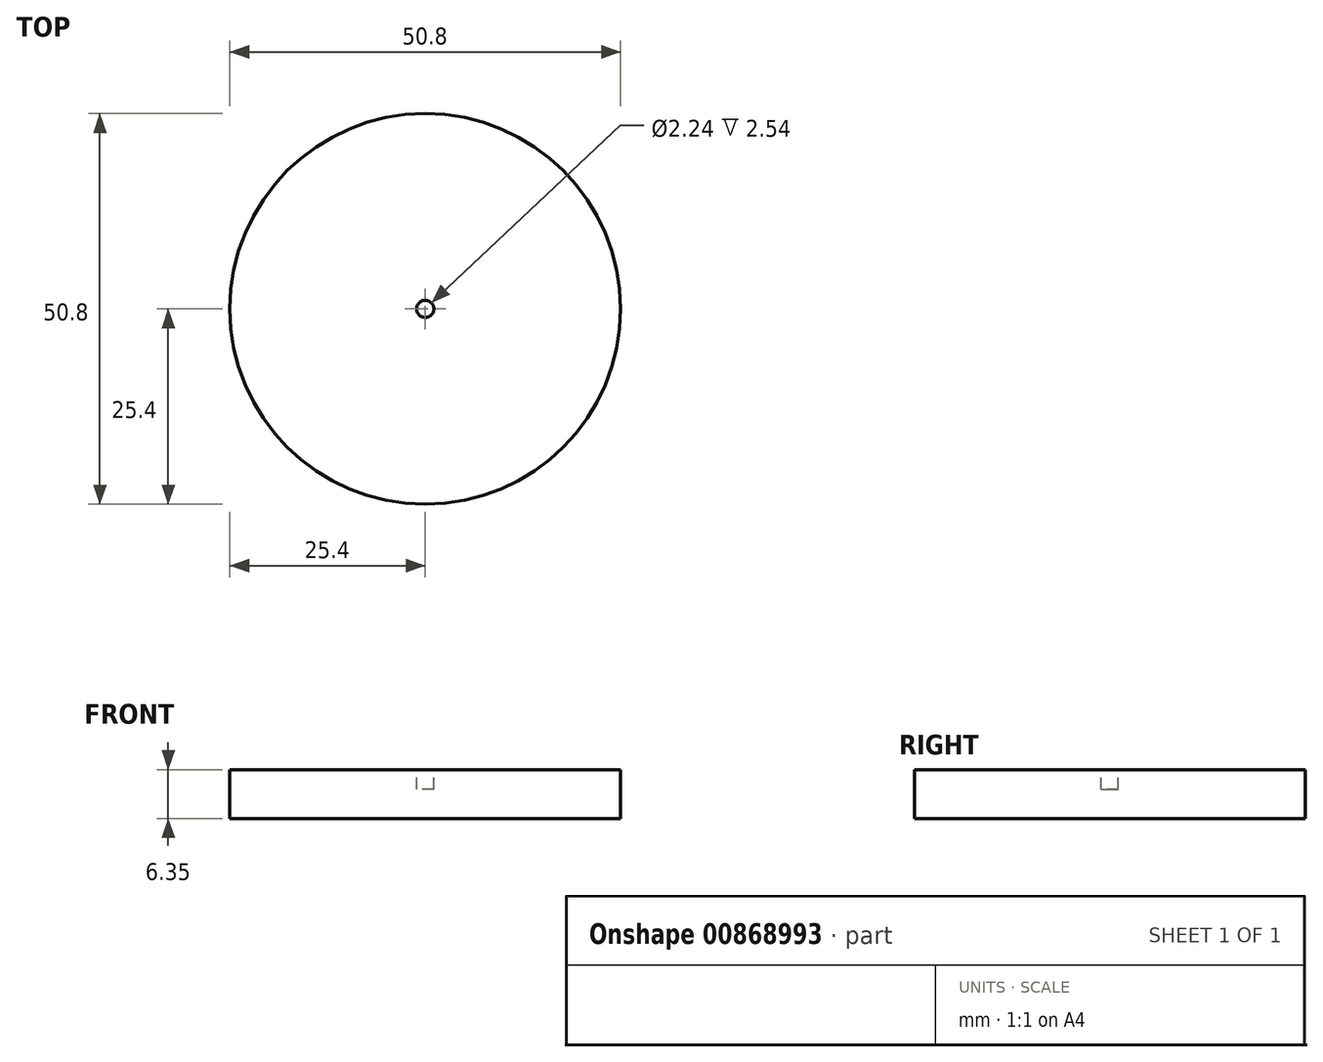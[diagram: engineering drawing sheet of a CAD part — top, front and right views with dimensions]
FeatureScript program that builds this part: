
annotation { "Feature Type Name" : "Feature", "Feature Type Description" : "" }
export const myFeature = defineFeature(function(context is Context, id is Id, definition is map)
    precondition{}
    {
        {
            var Q0;
            Q0=qCreatedBy(makeId("Top.planeOp"),FACE);
            var sketch = newSketch(context, id + "F0", { "sketchPlane" : qUnion([Q0])});
            skCircle(sketch, "E0", {"center": v(0, 0) * mm, "radius": 25.4 * mm});
            skSolve(sketch);
        }
        {
            var Q0;
            Q0=qSketchRegion(id+"F0",true);
            extrude(context, id + "F1", {"entities" : qUnion([Q0]), "depth" : 6.35 * mm, "offsetDistance" : 25.4 * mm});
        }
        {
            var Q0;
            Q0=makeQuery(id+"F1.opExtrude","CAP_FACE",FACE,{"disambiguationData":[OSD([sQuery(id+"F0.wireOp",EDGE,"E0")])],"isStart":false});
            var sketch = newSketch(context, id + "F2", { "sketchPlane" : qUnion([Q0])});
            skCircle(sketch, "E1", {"center": v(0, 0) * mm, "radius": 1.12 * mm});
            skSolve(sketch);
        }
        {
            var Q0;
            Q0 = qSketchRegion(id + "F2", true);
            extrude(context, id + "F3", {"entities" : qUnion([Q0]), "operationType" : NewBodyOperationType.REMOVE, "oppositeDirection" : true, "depth" : 2.54 * mm, "offsetDistance" : 25.4 * mm});
        }
    });
